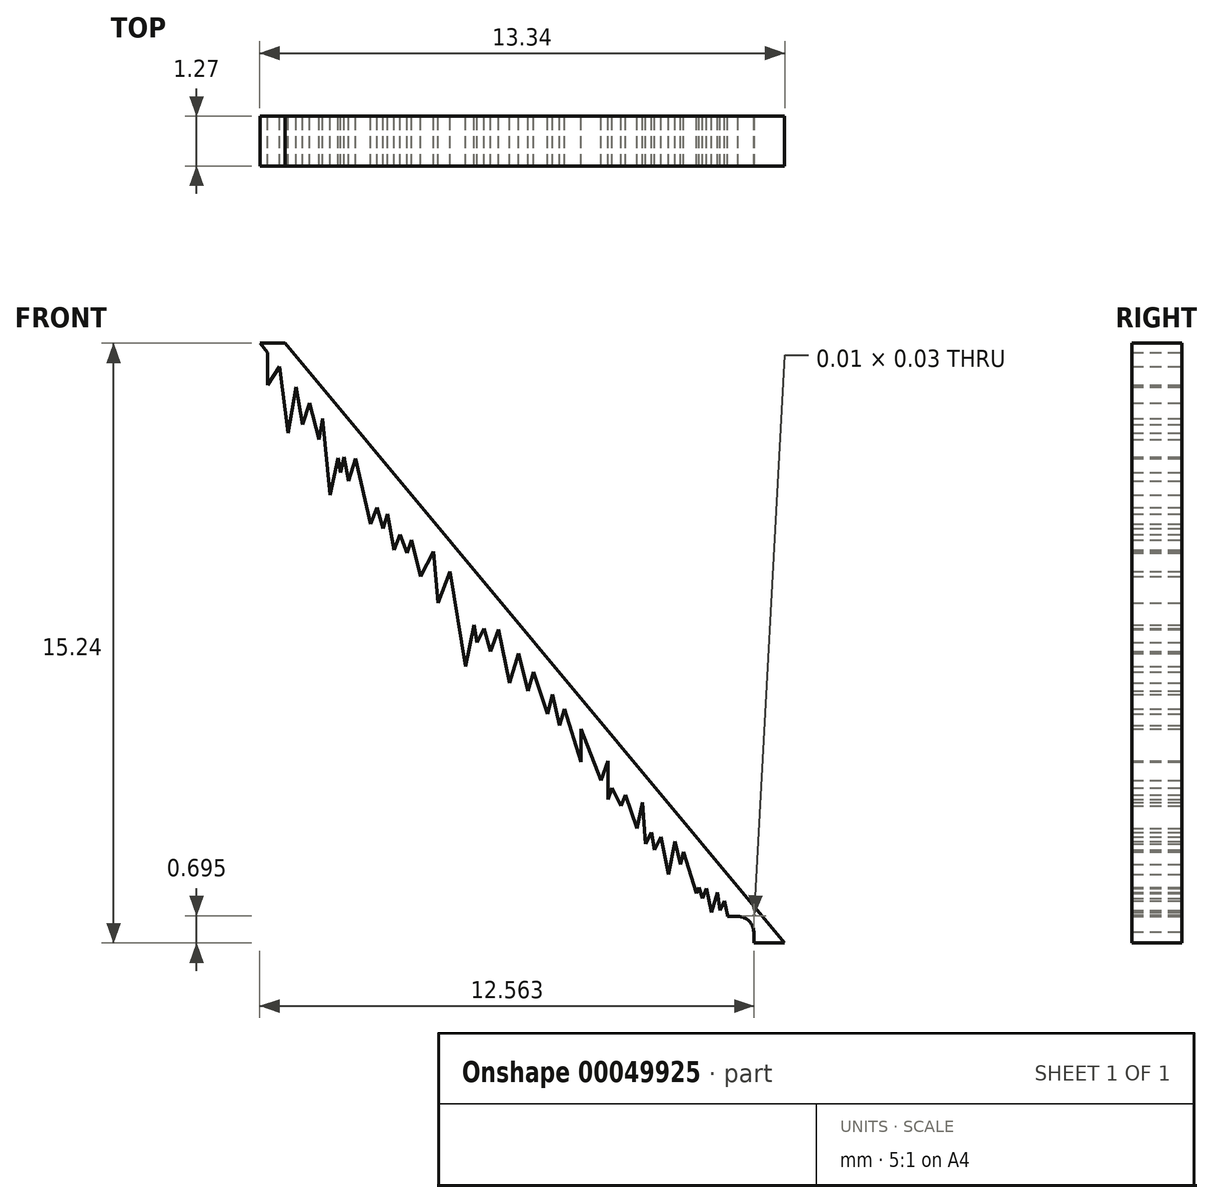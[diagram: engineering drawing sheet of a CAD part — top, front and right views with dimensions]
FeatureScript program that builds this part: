
annotation { "Feature Type Name" : "Feature", "Feature Type Description" : "" }
export const myFeature = defineFeature(function(context is Context, id is Id, definition is map)
    precondition{}
    {
        {
            var Q0;
            Q0=qCreatedBy(makeId("Front.planeOp"),FACE);
            var sketch = newSketch(context, id + "F0", { "sketchPlane" : qUnion([Q0])});
            skLineSegment(sketch, "E0", {"start": v(-0.87, 4.46) * mm, "end": v(11.83, -10.78) * mm});
            skLineSegment(sketch, "E1", {"start": v(11.83, -10.78) * mm, "end": v(11.2, -10.78) * mm});
            skLineSegment(sketch, "E2", {"start": v(-0.87, 4.46) * mm, "end": v(-1.5, 4.46) * mm});
            skLineSegment(sketch, "E3", {"start": v(9.78, -9.1) * mm, "end": v(9.59, -9.52) * mm});
            skLineSegment(sketch, "E4", {"start": v(9.59, -9.52) * mm, "end": v(9.26, -8.46) * mm});
            skLineSegment(sketch, "E5", {"start": v(9.26, -8.46) * mm, "end": v(9.18, -8.78) * mm});
            skLineSegment(sketch, "E6", {"start": v(9.18, -8.78) * mm, "end": v(9.04, -8.2) * mm});
            skLineSegment(sketch, "E7", {"start": v(9.04, -8.2) * mm, "end": v(8.87, -9.04) * mm});
            skLineSegment(sketch, "E8", {"start": v(8.87, -9.04) * mm, "end": v(8.6, -7.66) * mm});
            skLineSegment(sketch, "E9", {"start": v(8.6, -7.66) * mm, "end": v(8.3, -8.26) * mm});
            skLineSegment(sketch, "E10", {"start": v(8.3, -8.26) * mm, "end": v(8.21, -7.2) * mm});
            skLineSegment(sketch, "E11", {"start": v(8.21, -7.2) * mm, "end": v(8.07, -7.87) * mm});
            skLineSegment(sketch, "E12", {"start": v(8.07, -7.87) * mm, "end": v(7.58, -6.44) * mm});
            skLineSegment(sketch, "E13", {"start": v(7.58, -6.44) * mm, "end": v(7.34, -7.13) * mm});
            skLineSegment(sketch, "E14", {"start": v(7.34, -7.13) * mm, "end": v(7.34, -6.16) * mm});
            skLineSegment(sketch, "E15", {"start": v(7.34, -6.16) * mm, "end": v(7.16, -6.65) * mm});
            skLineSegment(sketch, "E16", {"start": v(7.16, -6.65) * mm, "end": v(6.65, -5.33) * mm});
            skLineSegment(sketch, "E17", {"start": v(6.65, -5.33) * mm, "end": v(6.65, -6.18) * mm});
            skLineSegment(sketch, "E18", {"start": v(6.65, -6.18) * mm, "end": v(6.24, -4.84) * mm});
            skLineSegment(sketch, "E19", {"start": v(6.24, -4.84) * mm, "end": v(6.1, -5.24) * mm});
            skLineSegment(sketch, "E20", {"start": v(6.1, -5.24) * mm, "end": v(5.92, -4.46) * mm});
            skLineSegment(sketch, "E21", {"start": v(5.92, -4.46) * mm, "end": v(5.8, -4.96) * mm});
            skLineSegment(sketch, "E22", {"start": v(5.8, -4.96) * mm, "end": v(5.45, -3.9) * mm});
            skLineSegment(sketch, "E23", {"start": v(5.45, -3.9) * mm, "end": v(5.3, -4.38) * mm});
            skLineSegment(sketch, "E24", {"start": v(5.3, -4.38) * mm, "end": v(5.06, -3.43) * mm});
            skLineSegment(sketch, "E25", {"start": v(5.06, -3.43) * mm, "end": v(4.83, -4.18) * mm});
            skLineSegment(sketch, "E26", {"start": v(4.83, -4.18) * mm, "end": v(4.55, -2.81) * mm});
            skLineSegment(sketch, "E27", {"start": v(4.55, -2.81) * mm, "end": v(4.35, -3.37) * mm});
            skLineSegment(sketch, "E28", {"start": v(4.35, -3.37) * mm, "end": v(4.04, -2.2) * mm});
            skLineSegment(sketch, "E29", {"start": v(4.04, -2.2) * mm, "end": v(3.71, -3.76) * mm});
            skLineSegment(sketch, "E30", {"start": v(3.71, -3.76) * mm, "end": v(3.32, -1.34) * mm});
            skLineSegment(sketch, "E31", {"start": v(3.32, -1.34) * mm, "end": v(3.02, -2.14) * mm});
            skLineSegment(sketch, "E32", {"start": v(3.02, -2.14) * mm, "end": v(2.9, -0.83) * mm});
            skLineSegment(sketch, "E33", {"start": v(2.9, -0.83) * mm, "end": v(2.58, -1.47) * mm});
            skLineSegment(sketch, "E34", {"start": v(2.58, -1.47) * mm, "end": v(2.2, 0) * mm});
            skLineSegment(sketch, "E35", {"start": v(2.2, 0) * mm, "end": v(1.9, -0.8) * mm});
            skLineSegment(sketch, "E36", {"start": v(1.9, -0.8) * mm, "end": v(1.63, 0.7) * mm});
            skLineSegment(sketch, "E37", {"start": v(1.63, 0.7) * mm, "end": v(1.3, -0.13) * mm});
            skLineSegment(sketch, "E38", {"start": v(1.3, -0.13) * mm, "end": v(0.93, 1.54) * mm});
            skLineSegment(sketch, "E39", {"start": v(0.93, 1.54) * mm, "end": v(0.74, 0.96) * mm});
            skLineSegment(sketch, "E40", {"start": v(0.74, 0.96) * mm, "end": v(0.57, 1.96) * mm});
            skLineSegment(sketch, "E41", {"start": v(0.57, 1.96) * mm, "end": v(0.28, 0.6) * mm});
            skLineSegment(sketch, "E42", {"start": v(0.28, 0.6) * mm, "end": v(0.1, 2.54) * mm});
            skLineSegment(sketch, "E43", {"start": v(0.1, 2.54) * mm, "end": v(0, 2) * mm});
            skLineSegment(sketch, "E44", {"start": v(0, 2) * mm, "end": v(-0.25, 2.95) * mm});
            skLineSegment(sketch, "E45", {"start": v(-0.25, 2.95) * mm, "end": v(-0.43, 2.4) * mm});
            skLineSegment(sketch, "E46", {"start": v(-0.43, 2.4) * mm, "end": v(-0.58, 3.35) * mm});
            skLineSegment(sketch, "E47", {"start": v(-0.58, 3.35) * mm, "end": v(-0.8, 2.18) * mm});
            skLineSegment(sketch, "E48", {"start": v(-0.8, 2.18) * mm, "end": v(-1, 3.86) * mm});
            skLineSegment(sketch, "E49", {"start": v(-1, 3.86) * mm, "end": v(-1.3, 3.4) * mm});
            skLineSegment(sketch, "E50", {"start": v(-1.3, 3.4) * mm, "end": v(-1.3, 4.22) * mm});
            skLineSegment(sketch, "E51", {"start": v(9.66, -9.37) * mm, "end": v(9.74, -9.64) * mm});
            skLineSegment(sketch, "E52", {"start": v(9.74, -9.64) * mm, "end": v(9.85, -9.4) * mm});
            skLineSegment(sketch, "E53", {"start": v(8.44, -7.96) * mm, "end": v(8.52, -8.41) * mm});
            skLineSegment(sketch, "E54", {"start": v(8.52, -8.41) * mm, "end": v(8.68, -8.09) * mm});
            skLineSegment(sketch, "E55", {"start": v(7.44, -6.84) * mm, "end": v(7.66, -7.3) * mm});
            skLineSegment(sketch, "E56", {"start": v(7.66, -7.3) * mm, "end": v(7.78, -7.02) * mm});
            skLineSegment(sketch, "E57", {"start": v(3.94, -2.7) * mm, "end": v(4, -3.14) * mm});
            skLineSegment(sketch, "E58", {"start": v(4, -3.14) * mm, "end": v(4.2, -2.78) * mm});
            skLineSegment(sketch, "E59", {"start": v(0.48, 1.55) * mm, "end": v(0.55, 1.18) * mm});
            skLineSegment(sketch, "E60", {"start": v(0.55, 1.18) * mm, "end": v(0.64, 1.57) * mm});
            skLineSegment(sketch, "E61", {"start": v(1.47, 0.28) * mm, "end": v(1.62, -0.24) * mm});
            skLineSegment(sketch, "E62", {"start": v(1.62, -0.24) * mm, "end": v(1.74, 0.12) * mm});
            skLineSegment(sketch, "E63", {"start": v(2.05, -0.4) * mm, "end": v(2.24, -0.87) * mm});
            skLineSegment(sketch, "E64", {"start": v(2.24, -0.87) * mm, "end": v(2.34, -0.53) * mm});
            skLineSegment(sketch, "E65", {"start": v(11.25, -10.18) * mm, "end": v(11.25, -10.78) * mm});
            skLineSegment(sketch, "E66", {"start": v(10.7, -10.18) * mm, "end": v(-1.5, 4.46) * mm});
            skLineSegment(sketch, "E67", {"start": v(9.78, -9.1) * mm, "end": v(9.85, -9.4) * mm});
            skLineSegment(sketch, "E68", {"start": v(9.78, -9.1) * mm, "end": v(9.97, -10) * mm});
            skLineSegment(sketch, "E69", {"start": v(9.97, -10) * mm, "end": v(10.12, -9.5) * mm});
            skLineSegment(sketch, "E70", {"start": v(10.12, -9.5) * mm, "end": v(10.18, -9.95) * mm});
            skLineSegment(sketch, "E71", {"start": v(10.18, -9.95) * mm, "end": v(10.3, -9.7) * mm});
            skLineSegment(sketch, "E72", {"start": v(11.2, -10.78) * mm, "end": v(11.06, -10.78) * mm});
            skLineSegment(sketch, "E73", {"start": v(11.06, -10.78) * mm, "end": v(11.06, -10.2) * mm});
            skLineSegment(sketch, "E74", {"start": v(11.06, -10.2) * mm, "end": v(11.06, -10.18) * mm});
            skLineSegment(sketch, "E75", {"start": v(11.06, -10.18) * mm, "end": v(11.06, -10.07) * mm});
            skLineSegment(sketch, "E76", {"start": v(11.06, -10.07) * mm, "end": v(10.38, -10.07) * mm});
            skLineSegment(sketch, "E77", {"start": v(10.3, -9.7) * mm, "end": v(10.38, -10.07) * mm});
            skLineSegment(sketch, "E78", {"start": v(10.38, -10.07) * mm, "end": v(10.38, -10.1) * mm});
            skLineSegment(sketch, "E79", {"start": v(10.38, -10.1) * mm, "end": v(11.06, -10.1) * mm});
            skLineSegment(sketch, "E80", {"start": v(11.06, -10.78) * mm, "end": v(11.05, -10.78) * mm});
            skLineSegment(sketch, "E81", {"start": v(11.05, -10.78) * mm, "end": v(11.05, -10.07) * mm});
            skArc(sketch, "E82", {"start": v(11.05, -10.56) * mm, "mid": v(10.94, -10.24) * mm, "end": v(10.64, -10.1) * mm});
            skSolve(sketch);
        }
        {
            var Q0;
            Q0 = qSketchRegion(id + "F0", true);
            extrude(context, id + "F1", {"entities" : qUnion([Q0]), "depth" : 1.27 * mm});
        }
    });
